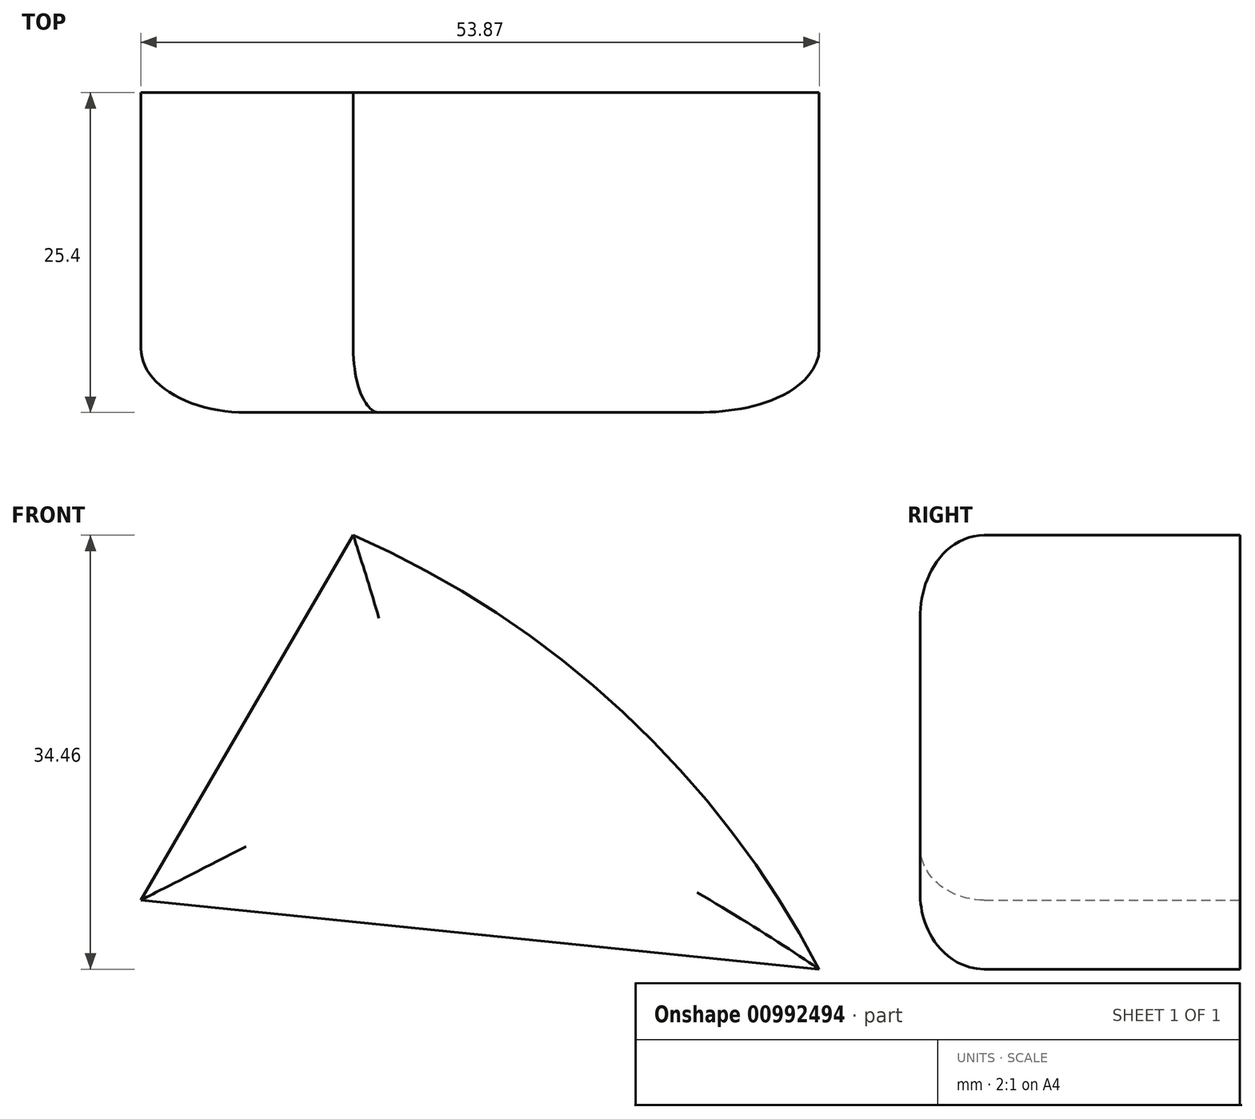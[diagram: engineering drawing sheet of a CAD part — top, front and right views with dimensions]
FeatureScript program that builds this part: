
annotation { "Feature Type Name" : "Feature", "Feature Type Description" : "" }
export const myFeature = defineFeature(function(context is Context, id is Id, definition is map)
    precondition{}
    {
        {
            var Q0;
            Q0=qCreatedBy(makeId("Front.planeOp"),FACE);
            var sketch = newSketch(context, id + "F0", { "sketchPlane" : qUnion([Q0])});
            skLineSegment(sketch, "E0", {"start": v(0, 0) * mm, "end": v(62.57, -6.37) * mm});
            skLineSegment(sketch, "E1", {"start": v(62.57, -6.37) * mm, "end": v(62.57, 25.07) * mm});
            skLineSegment(sketch, "E2", {"start": v(62.57, 25.07) * mm, "end": v(16.86, 28.98) * mm});
            skLineSegment(sketch, "E3", {"start": v(16.86, 28.98) * mm, "end": v(0, 0) * mm});
            skSolve(sketch);
        }
        {
            var Q0;
            Q0=makeQuery(id+"F0.imprint","IMPRINT",FACE,{"disambiguationData":[TD([[makeQuery(id+"F0.imprint","IMPRINT",EDGE,{"derivedFrom":sQuery(id+"F0.wireOp",EDGE,"E0")}),1.0]])]});
            extrude(context, id + "F1", {"entities" : qUnion([Q0]), "depth" : 25.4 * mm, "offsetDistance" : 25.4 * mm});
        }
        {
            var Q0;
            Q0=makeQuery(id+"F1.opExtrude","SWEPT_EDGE",EDGE,{"disambiguationData":[OSD([sQuery(id+"F0.wireOp",EDGE,"E1"),sQuery(id+"F0.wireOp",EDGE,"E2")])]});
            fillet(context, id + "F2", {"entities" : qUnion([Q0]), "radius" : 76.2 * mm, "tangentPropagation" : true, "allowEdgeOverflow" : false});
        }
        {
            var Q0;
            Q0=makeQuery(id+"F1.opExtrude","CAP_FACE",FACE,{"disambiguationData":[OSD([sQuery(id+"F0.wireOp",EDGE,"E0"),sQuery(id+"F0.wireOp",EDGE,"E1"),sQuery(id+"F0.wireOp",EDGE,"E2"),sQuery(id+"F0.wireOp",EDGE,"E3")])],"isStart":false});
            fillet(context, id + "F3", {"entities" : qUnion([Q0]), "radius" : 5.08 * mm, "tangentPropagation" : true, "allowEdgeOverflow" : false});
        }
    });
